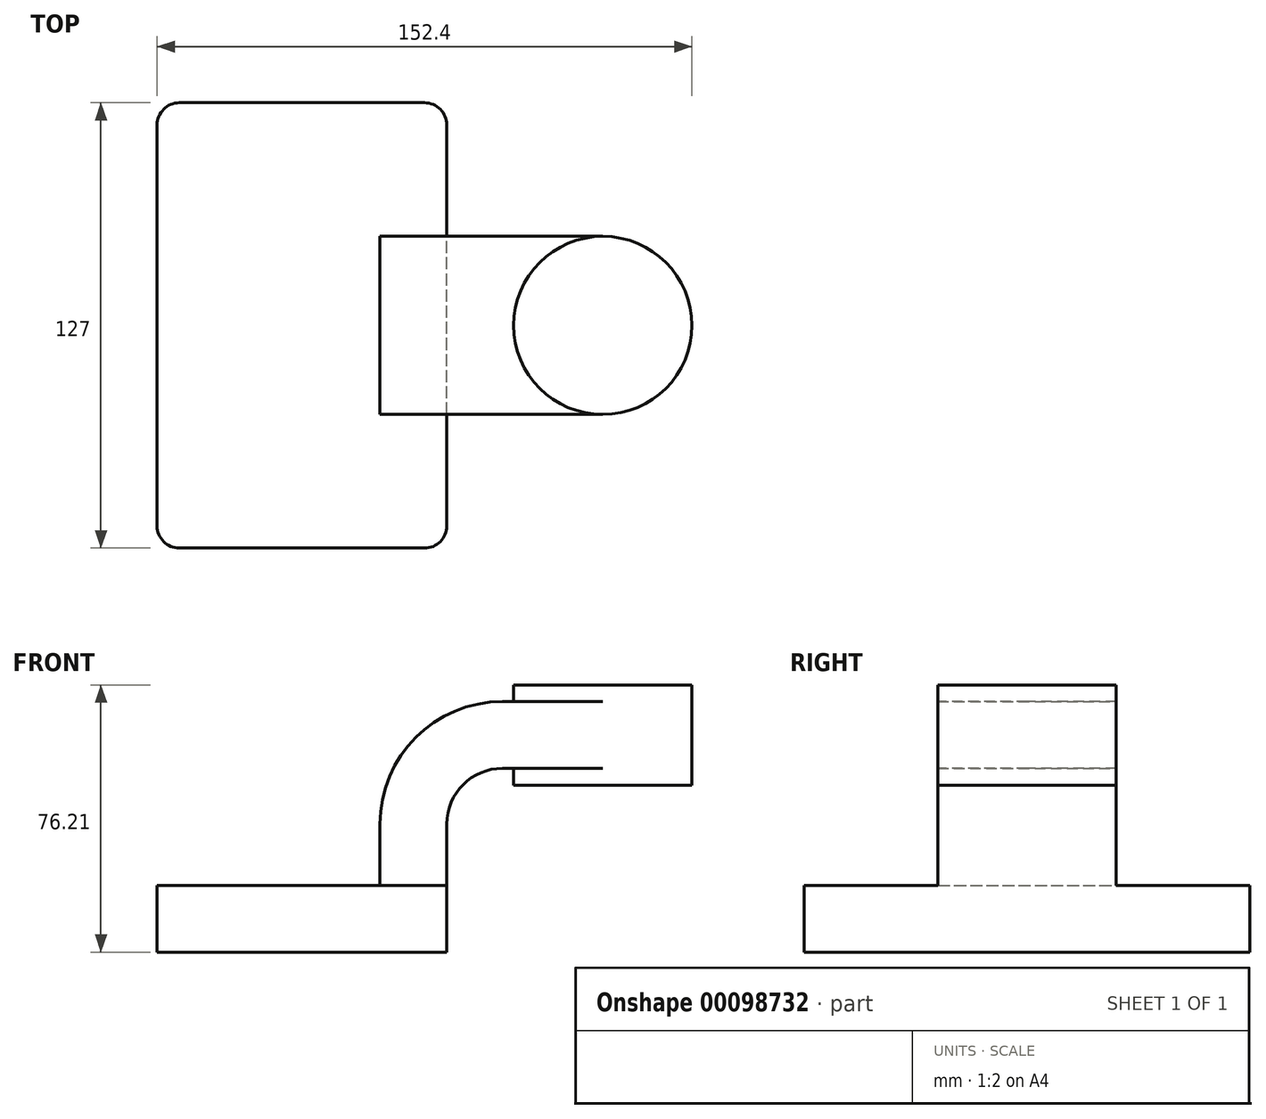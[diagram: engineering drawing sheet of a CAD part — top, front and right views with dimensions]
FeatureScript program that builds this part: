
annotation { "Feature Type Name" : "Feature", "Feature Type Description" : "" }
export const myFeature = defineFeature(function(context is Context, id is Id, definition is map)
    precondition{}
    {
        {
            var Q0;
            Q0=qCreatedBy(makeId("Front.planeOp"),FACE);
            var sketch = newSketch(context, id + "F0", { "sketchPlane" : qUnion([Q0])});
            skLineSegment(sketch, "E0.bottom", {"start": v(41.27, 9.53) * mm, "end": v(-41.28, 9.53) * mm});
            skLineSegment(sketch, "E0.top", {"start": v(41.28, -9.52) * mm, "end": v(-41.27, -9.52) * mm});
            skLineSegment(sketch, "E0.left", {"start": v(41.28, 9.53) * mm, "end": v(41.28, -9.52) * mm});
            skLineSegment(sketch, "E0.right", {"start": v(-41.28, 9.53) * mm, "end": v(-41.27, -9.52) * mm});
            skPoint(sketch, "E0.middle", {"position": v(0, 0) * mm});
            skLineSegment(sketch, "E1", {"start": v(41.27, 9.53) * mm, "end": v(41.27, 27) * mm});
            skLineSegment(sketch, "E2.bottom", {"start": v(60.32, 66.68) * mm, "end": v(111.12, 66.68) * mm});
            skLineSegment(sketch, "E2.top", {"start": v(60.33, 38.1) * mm, "end": v(111.12, 38.1) * mm});
            skLineSegment(sketch, "E2.left", {"start": v(60.32, 66.68) * mm, "end": v(60.33, 38.1) * mm});
            skLineSegment(sketch, "E2.right", {"start": v(111.12, 66.68) * mm, "end": v(111.12, 38.1) * mm});
            skPoint(sketch, "E2.middle", {"position": v(85.72, 52.39) * mm});
            skArc(sketch, "E3", {"start": v(41.27, 27) * mm, "mid": v(45.92, 38.23) * mm, "end": v(57.15, 42.88) * mm});
            skLineSegment(sketch, "E4", {"start": v(57.15, 42.88) * mm, "end": v(67.87, 42.88) * mm});
            skLineSegment(sketch, "E5.0", {"start": v(57.15, 61.93) * mm, "end": v(67.87, 61.93) * mm});
            skArc(sketch, "E5.1", {"start": v(22.22, 27) * mm, "mid": v(32.45, 51.7) * mm, "end": v(57.15, 61.93) * mm});
            skLineSegment(sketch, "E5.2", {"start": v(22.22, 9.53) * mm, "end": v(22.22, 27) * mm});
            skLineSegment(sketch, "E6", {"start": v(85.72, 38.1) * mm, "end": v(85.72, 66.68) * mm});
            skFitSpline(sketch, "E7", {"points": [v(-41.28, 9.52) * mm, v(57.15, 61.93) * mm], "startDerivative": vector(2.3, 156.24) * mm, "endDerivative": vector(88.25, -0.15) * mm});
            skLineSegment(sketch, "E8", {"start": v(67.87, 61.93) * mm, "end": v(85.72, 61.93) * mm});
            skLineSegment(sketch, "E9", {"start": v(67.87, 42.88) * mm, "end": v(85.72, 42.88) * mm});
            skSolve(sketch);
        }
        {
            var Q0;
            Q0=makeQuery(id+"F0.imprint","IMPRINT",FACE,{"disambiguationData":[TD([[makeQuery(id+"F0.imprint","IMPRINT",EDGE,{"derivedFrom":sQuery(id+"F0.wireOp",EDGE,"E0.top")}),-1.0]])]});
            extrude(context, id + "F1", {"entities" : qUnion([Q0]), "endBound" : BoundingType.SYMMETRIC, "depth" : 127 * mm});
        }
        {
            var Q0;
            {var subQ6=sQuery(id+"F0.wireOp",EDGE,"E1");Q0=makeQuery(id+"F0.imprint","IMPRINT",FACE,{"disambiguationData":[TD([[makeQuery(id+"F0.imprint","IMPRINT",EDGE,{"derivedFrom":subQ6}),1.0]])]});}
            var Q1;
            {var subQ0=sQuery(id+"F0.wireOp",EDGE,"E8");Q1=makeQuery(id+"F0.imprint","IMPRINT",FACE,{"disambiguationData":[TD([[makeQuery(id+"F0.imprint","IMPRINT",EDGE,{"derivedFrom":subQ0}),-1.0]])]});}
            extrude(context, id + "F2", {"entities" : qUnion([Q0, Q1]), "operationType" : NewBodyOperationType.ADD, "endBound" : BoundingType.SYMMETRIC, "depth" : 50.8 * mm});
        }
        {
            var Q0;
            Q0=makeQuery(id+"F0.imprint","IMPRINT",FACE,{"disambiguationData":[TD([[makeQuery(id+"F0.imprint","IMPRINT",EDGE,{"derivedFrom":sQuery(id+"F0.wireOp",EDGE,"E5.1")}),1.0]])]});
            extrude(context, id + "F3", {"entities" : qUnion([Q0]), "operationType" : NewBodyOperationType.ADD, "endBound" : BoundingType.SYMMETRIC, "depth" : 15.88 * mm});
        }
        {
            var Q0;
            {var subQ0=sQuery(id+"F0.wireOp",EDGE,"E2.right");Q0=makeQuery(id+"F0.imprint","IMPRINT",FACE,{"disambiguationData":[TD([[makeQuery(id+"F0.imprint","IMPRINT",EDGE,{"derivedFrom":subQ0}),-1.0]])]});}
            var Q1;
            Q1=sQuery(id+"F0.wireOp",EDGE,"E6");
            revolve(context, id + "F4", {"operationType" : NewBodyOperationType.ADD, "entities" : qUnion([Q0]), "axis" : qUnion([Q1]), "revolveType" : RevolveType.FULL});
        }
        {
            var Q0;
            Q0=makeQuery(id+"F1.opExtrude","CAP_EDGE",EDGE,{"disambiguationData":[OSD([sQuery(id+"F0.wireOp",EDGE,"E0.left")])],"isStart":false});
            var Q1;
            Q1=makeQuery(id+"F1.opExtrude","CAP_EDGE",EDGE,{"disambiguationData":[OSD([sQuery(id+"F0.wireOp",EDGE,"E0.right")])],"isStart":false});
            var Q2;
            Q2=makeQuery(id+"F1.opExtrude","CAP_EDGE",EDGE,{"disambiguationData":[OSD([sQuery(id+"F0.wireOp",EDGE,"E0.left")])],"isStart":true});
            var Q3;
            Q3=makeQuery(id+"F1.opExtrude","CAP_EDGE",EDGE,{"disambiguationData":[OSD([sQuery(id+"F0.wireOp",EDGE,"E0.right")])],"isStart":true});
            fillet(context, id + "F5", {"entities" : qUnion([Q0, Q1, Q2, Q3]), "radius" : 6.35 * mm, "tangentPropagation" : true, "allowEdgeOverflow" : false});
        }
    });
